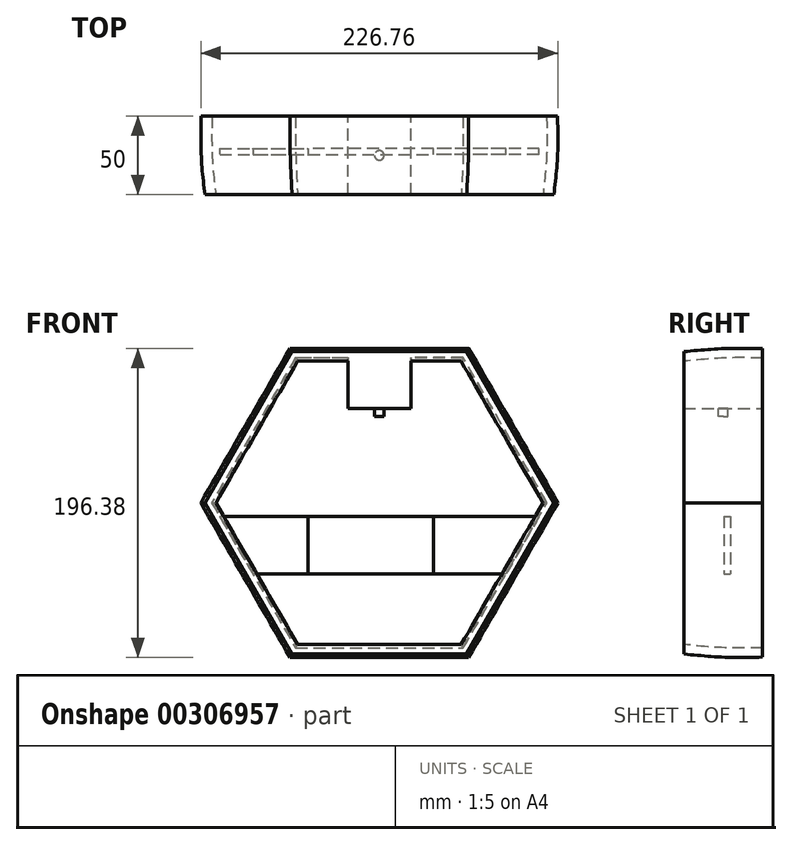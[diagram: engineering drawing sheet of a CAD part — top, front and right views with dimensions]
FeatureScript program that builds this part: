
annotation { "Feature Type Name" : "Feature", "Feature Type Description" : "" }
export const myFeature = defineFeature(function(context is Context, id is Id, definition is map)
    precondition{}
    {
        {
            var Q0;
            Q0=qCreatedBy(makeId("Front.planeOp"),FACE);
            var sketch = newSketch(context, id + "F0", { "sketchPlane" : qUnion([Q0])});
            skCircle(sketch, "E0.cCircle", {"center": v(0, 0) * mm, "radius": 98 * mm, "construction": true});
            skLineSegment(sketch, "E0.0", {"start": v(-56.58, 98) * mm, "end": v(56.58, 98) * mm});
            skLineSegment(sketch, "E0.1", {"start": v(56.58, 98) * mm, "end": v(113.16, 0) * mm});
            skLineSegment(sketch, "E0.2", {"start": v(113.16, 0) * mm, "end": v(56.58, -98) * mm});
            skLineSegment(sketch, "E0.3", {"start": v(56.58, -98) * mm, "end": v(-56.58, -98) * mm});
            skLineSegment(sketch, "E0.4", {"start": v(-56.58, -98) * mm, "end": v(-113.16, 0) * mm});
            skLineSegment(sketch, "E0.5", {"start": v(-113.16, 0) * mm, "end": v(-56.58, 98) * mm});
            skPoint(sketch, "E0.0.midPoint", {"position": v(0, 98) * mm});
            skSolve(sketch);
        }
        {
            var Q0;
            Q0=qCreatedBy(makeId("Front.planeOp"),FACE);
            cPlane(context, id + "F1", {"entities" : qUnion([Q0]), "cplaneType" : CPlaneType.OFFSET, "offset" : 25 * mm, "oppositeDirection" : true, "width" : 150 * mm, "height" : 150 * mm});
        }
        {
            var Q0;
            Q0=qCreatedBy(id+"F1.planeOp",FACE);
            var sketch = newSketch(context, id + "F2", { "sketchPlane" : qUnion([Q0])});
            skCircle(sketch, "E1.cCircle", {"center": v(0, 0) * mm, "radius": 98 * mm, "construction": true});
            skLineSegment(sketch, "E1.0", {"start": v(-56.58, 98) * mm, "end": v(56.58, 98) * mm});
            skLineSegment(sketch, "E1.1", {"start": v(56.58, 98) * mm, "end": v(113.16, 0) * mm});
            skLineSegment(sketch, "E1.2", {"start": v(113.16, 0) * mm, "end": v(56.58, -98) * mm});
            skLineSegment(sketch, "E1.3", {"start": v(56.58, -98) * mm, "end": v(-56.58, -98) * mm});
            skLineSegment(sketch, "E1.4", {"start": v(-56.58, -98) * mm, "end": v(-113.16, 0) * mm});
            skLineSegment(sketch, "E1.5", {"start": v(-113.16, 0) * mm, "end": v(-56.58, 98) * mm});
            skPoint(sketch, "E1.0.midPoint", {"position": v(0, 98) * mm});
            skSolve(sketch);
        }
        {
            var Q0;
            Q0=qCreatedBy(makeId("Front.planeOp"),FACE);
            cPlane(context, id + "F3", {"entities" : qUnion([Q0]), "cplaneType" : CPlaneType.OFFSET, "offset" : 25 * mm, "width" : 150 * mm, "height" : 150 * mm});
        }
        {
            var Q0;
            Q0=qCreatedBy(id+"F3.planeOp",FACE);
            var sketch = newSketch(context, id + "F4", { "sketchPlane" : qUnion([Q0])});
            skCircle(sketch, "E2.cCircle", {"center": v(0, 0) * mm, "radius": 96 * mm, "construction": true});
            skLineSegment(sketch, "E2.0", {"start": v(55.43, -96) * mm, "end": v(-55.43, -96) * mm});
            skLineSegment(sketch, "E2.1", {"start": v(-55.43, -96) * mm, "end": v(-110.85, 0) * mm});
            skLineSegment(sketch, "E2.2", {"start": v(-110.85, 0) * mm, "end": v(-55.43, 96) * mm});
            skLineSegment(sketch, "E2.3", {"start": v(-55.43, 96) * mm, "end": v(55.43, 96) * mm});
            skLineSegment(sketch, "E2.4", {"start": v(55.43, 96) * mm, "end": v(110.85, 0) * mm});
            skLineSegment(sketch, "E2.5", {"start": v(110.85, 0) * mm, "end": v(55.43, -96) * mm});
            skPoint(sketch, "E2.0.midPoint", {"position": v(0, -96) * mm});
            skSolve(sketch);
        }
        {
            var Q0;
            Q0=makeQuery(id+"F2.imprint","IMPRINT",FACE,{"disambiguationData":[TD([[makeQuery(id+"F2.imprint","IMPRINT",EDGE,{"derivedFrom":sQuery(id+"F2.wireOp",EDGE,"E1.0")}),-1.0]])]});
            var Q1;
            Q1=makeQuery(id+"F0.imprint","IMPRINT",FACE,{"disambiguationData":[TD([[makeQuery(id+"F0.imprint","IMPRINT",EDGE,{"derivedFrom":sQuery(id+"F0.wireOp",EDGE,"E0.0")}),-1.0]])]});
            var Q2;
            Q2=makeQuery(id+"F4.imprint","IMPRINT",FACE,{"disambiguationData":[TD([[makeQuery(id+"F4.imprint","IMPRINT",EDGE,{"derivedFrom":sQuery(id+"F4.wireOp",EDGE,"E2.0")}),-1.0]])]});
            loft(context, id + "F5", {"sheetProfilesArray" : [{ "sheetProfileEntities" : qUnion([Q0]) }, { "sheetProfileEntities" : qUnion([Q1]) }, { "sheetProfileEntities" : qUnion([Q2]) }]});
        }
        {
            var Q0;
            Q0=makeQuery(id+"F5.opLoft","CAP_FACE",FACE,{"disambiguationData":[OSD([makeQuery(id+"F2.imprint","IMPRINT",FACE,{"disambiguationData":[TD([[makeQuery(id+"F2.imprint","IMPRINT",EDGE,{"derivedFrom":sQuery(id+"F2.wireOp",EDGE,"E1.0")}),-1.0]])]})])],"isStart":true});
            var Q1;
            Q1=makeQuery(id+"F5.opLoft","CAP_FACE",FACE,{"disambiguationData":[OSD([makeQuery(id+"F4.imprint","IMPRINT",FACE,{"disambiguationData":[TD([[makeQuery(id+"F4.imprint","IMPRINT",EDGE,{"derivedFrom":sQuery(id+"F4.wireOp",EDGE,"E2.0")}),-1.0]])]})])],"isStart":true});
            shell(context, id + "F6", {"entities" : qUnion([Q0, Q1]), "thickness" : 6 * mm});
        }
        {
            var Q0;
            Q0=qCreatedBy(makeId("Top.planeOp"),FACE);
            cPlane(context, id + "F7", {"entities" : qUnion([Q0]), "cplaneType" : CPlaneType.OFFSET, "offset" : 45 * mm, "oppositeDirection" : true, "width" : 150 * mm, "height" : 150 * mm});
        }
        {
            var Q0;
            Q0=qCreatedBy(id+"F7.planeOp",FACE);
            var sketch = newSketch(context, id + "F8", { "sketchPlane" : qUnion([Q0])});
            skLineSegment(sketch, "E3", {"start": v(34.28, 4.44) * mm, "end": v(-45.28, 4.44) * mm});
            skLineSegment(sketch, "E4", {"start": v(-45.28, 4.44) * mm, "end": v(-45.28, 0.44) * mm});
            skLineSegment(sketch, "E5", {"start": v(-45.28, 0.44) * mm, "end": v(34.28, 0.44) * mm});
            skLineSegment(sketch, "E6", {"start": v(34.28, 0.44) * mm, "end": v(34.28, 4.44) * mm});
            skSolve(sketch);
        }
        {
            var Q0;
            Q0 = qSketchRegion(id + "F8", true);
            extrude(context, id + "F9", {"entities" : qUnion([Q0]), "depth" : 36.5 * mm});
        }
        {
            var Q0;
            Q0=makeQuery(id+"F9.opExtrude","SWEPT_FACE",FACE,{"disambiguationData":[OSD([sQuery(id+"F8.wireOp",EDGE,"E4")])]});
            extrude(context, id + "F10", {"entities" : qUnion([Q0]), "endBound" : BoundingType.UP_TO_NEXT, "depth" : 25 * mm});
        }
        {
            var Q0;
            Q0=makeQuery(id+"F9.opExtrude","SWEPT_FACE",FACE,{"disambiguationData":[OSD([sQuery(id+"F8.wireOp",EDGE,"E6")])]});
            extrude(context, id + "F11", {"entities" : qUnion([Q0]), "endBound" : BoundingType.UP_TO_NEXT, "depth" : 25 * mm});
        }
        {
            var Q0;
            Q0=qCreatedBy(makeId("Top.planeOp"),FACE);
            cPlane(context, id + "F12", {"entities" : qUnion([Q0]), "cplaneType" : CPlaneType.OFFSET, "offset" : 60 * mm, "width" : 150 * mm, "height" : 150 * mm});
        }
        {
            var Q0;
            Q0=qCreatedBy(id+"F12.planeOp",FACE);
            var sketch = newSketch(context, id + "F13", { "sketchPlane" : qUnion([Q0])});
            skLineSegment(sketch, "E7.0", {"start": v(20, -25) * mm, "end": v(-20, -25) * mm});
            skLineSegment(sketch, "E8.0", {"start": v(20, 25) * mm, "end": v(-20, 25) * mm});
            skLineSegment(sketch, "E9", {"start": v(-20, -25) * mm, "end": v(-20, 25) * mm});
            skLineSegment(sketch, "E10", {"start": v(20, -25) * mm, "end": v(20, 25) * mm});
            skPoint(sketch, "E11.orphan", {"position": v(-56.58, 25) * mm});
            skPoint(sketch, "E12.orphan", {"position": v(-55.43, -25) * mm});
            skPoint(sketch, "E13.orphan", {"position": v(55.43, -25) * mm});
            skPoint(sketch, "E14.orphan", {"position": v(56.58, 25) * mm});
            skSolve(sketch);
        }
        {
            var Q0;
            Q0 = qSketchRegion(id + "F13", true);
            extrude(context, id + "F14", {"entities" : qUnion([Q0]), "operationType" : NewBodyOperationType.ADD, "endBound" : BoundingType.UP_TO_NEXT, "depth" : 25 * mm});
        }
        {
            var Q0;
            Q0=makeQuery(id+"F14.opExtrude","CAP_FACE",FACE,{"disambiguationData":[OSD([sQuery(id+"F13.wireOp",EDGE,"E7.0"),sQuery(id+"F13.wireOp",EDGE,"E8.0"),sQuery(id+"F13.wireOp",EDGE,"E9"),sQuery(id+"F13.wireOp",EDGE,"E10")])],"isStart":true});
            var sketch = newSketch(context, id + "F15", { "sketchPlane" : qUnion([Q0])});
            skCircle(sketch, "E15", {"center": v(0, 0) * mm, "radius": 3 * mm});
            skSolve(sketch);
        }
        {
            var Q0;
            Q0 = qSketchRegion(id + "F15", true);
            extrude(context, id + "F16", {"entities" : qUnion([Q0]), "operationType" : NewBodyOperationType.ADD, "depth" : 5 * mm});
        }
    });
